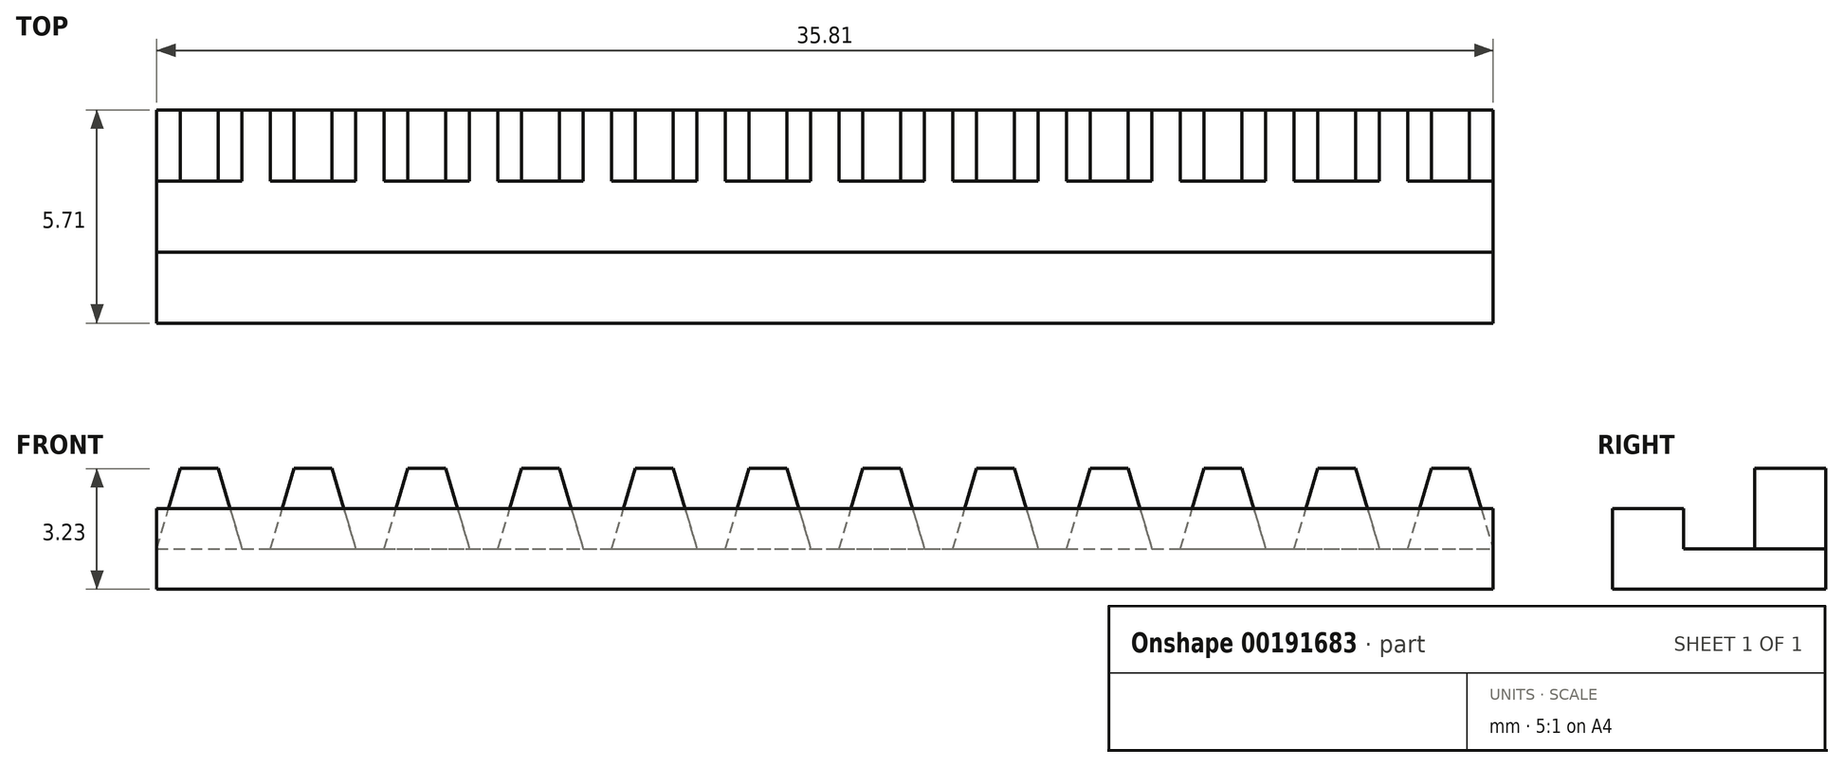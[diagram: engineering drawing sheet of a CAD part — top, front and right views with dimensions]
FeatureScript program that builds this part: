
annotation { "Feature Type Name" : "Feature", "Feature Type Description" : "" }
export const myFeature = defineFeature(function(context is Context, id is Id, definition is map)
    precondition{}
    {
        {
            var Q0;
            Q0=qCreatedBy(makeId("Front.planeOp"),FACE);
            var sketch = newSketch(context, id + "F0", { "sketchPlane" : qUnion([Q0])});
            skLineSegment(sketch, "E0.bottom", {"start": v(-38.44, 14.74) * mm, "end": v(33.18, 14.74) * mm});
            skLineSegment(sketch, "E0.top", {"start": v(-38.44, 16.9) * mm, "end": v(33.18, 16.9) * mm});
            skLineSegment(sketch, "E0.left", {"start": v(-38.44, 14.74) * mm, "end": v(-38.44, 16.9) * mm});
            skLineSegment(sketch, "E1", {"start": v(-38.44, 16.9) * mm, "end": v(-37.17, 21.21) * mm});
            skLineSegment(sketch, "E2", {"start": v(-37.17, 21.21) * mm, "end": v(-35.14, 21.21) * mm});
            skLineSegment(sketch, "E3", {"start": v(-35.14, 21.21) * mm, "end": v(-33.87, 16.9) * mm});
            skLineSegment(sketch, "E4", {"start": v(-38.44, 16.9) * mm, "end": v(-33.87, 16.9) * mm});
            skLineSegment(sketch, "E5", {"start": v(-36.16, 21.21) * mm, "end": v(-36.16, 16.9) * mm, "construction": true});
            skLineSegment(sketch, "E6", {"start": v(33.18, 14.74) * mm, "end": v(33.18, 16.9) * mm});
            skLineSegment(sketch, "E7.1.0.0", {"start": v(-29.05, 21.21) * mm, "end": v(-27.78, 16.9) * mm});
            skLineSegment(sketch, "E7.1.0.1", {"start": v(-32.35, 16.9) * mm, "end": v(-31.08, 21.21) * mm});
            skLineSegment(sketch, "E7.1.0.2", {"start": v(-31.08, 21.21) * mm, "end": v(-29.05, 21.21) * mm});
            skLineSegment(sketch, "E7.2.0.0", {"start": v(-22.95, 21.21) * mm, "end": v(-21.68, 16.9) * mm});
            skLineSegment(sketch, "E7.2.0.1", {"start": v(-26.25, 16.9) * mm, "end": v(-24.98, 21.21) * mm});
            skLineSegment(sketch, "E7.2.0.2", {"start": v(-24.98, 21.21) * mm, "end": v(-22.95, 21.21) * mm});
            skLineSegment(sketch, "E7.3.0.0", {"start": v(-16.85, 21.21) * mm, "end": v(-15.58, 16.9) * mm});
            skLineSegment(sketch, "E7.3.0.1", {"start": v(-20.16, 16.9) * mm, "end": v(-18.89, 21.21) * mm});
            skLineSegment(sketch, "E7.3.0.2", {"start": v(-18.89, 21.21) * mm, "end": v(-16.85, 21.21) * mm});
            skLineSegment(sketch, "E7.4.0.0", {"start": v(-10.76, 21.21) * mm, "end": v(-9.49, 16.9) * mm});
            skLineSegment(sketch, "E7.4.0.1", {"start": v(-14.06, 16.9) * mm, "end": v(-12.8, 21.21) * mm});
            skLineSegment(sketch, "E7.4.0.2", {"start": v(-12.8, 21.21) * mm, "end": v(-10.76, 21.21) * mm});
            skLineSegment(sketch, "E7.5.0.0", {"start": v(-4.66, 21.21) * mm, "end": v(-3.4, 16.9) * mm});
            skLineSegment(sketch, "E7.5.0.1", {"start": v(-7.96, 16.9) * mm, "end": v(-6.7, 21.21) * mm});
            skLineSegment(sketch, "E7.5.0.2", {"start": v(-6.7, 21.21) * mm, "end": v(-4.66, 21.21) * mm});
            skLineSegment(sketch, "E7.6.0.0", {"start": v(1.43, 21.21) * mm, "end": v(2.7, 16.9) * mm});
            skLineSegment(sketch, "E7.6.0.1", {"start": v(-1.87, 16.9) * mm, "end": v(-0.6, 21.21) * mm});
            skLineSegment(sketch, "E7.6.0.2", {"start": v(-0.6, 21.21) * mm, "end": v(1.43, 21.21) * mm});
            skLineSegment(sketch, "E7.7.0.0", {"start": v(7.53, 21.21) * mm, "end": v(8.8, 16.9) * mm});
            skLineSegment(sketch, "E7.7.0.1", {"start": v(4.23, 16.9) * mm, "end": v(5.5, 21.21) * mm});
            skLineSegment(sketch, "E7.7.0.2", {"start": v(5.5, 21.21) * mm, "end": v(7.53, 21.21) * mm});
            skLineSegment(sketch, "E7.8.0.0", {"start": v(13.63, 21.21) * mm, "end": v(14.9, 16.9) * mm});
            skLineSegment(sketch, "E7.8.0.1", {"start": v(10.32, 16.9) * mm, "end": v(11.6, 21.21) * mm});
            skLineSegment(sketch, "E7.8.0.2", {"start": v(11.6, 21.21) * mm, "end": v(13.63, 21.21) * mm});
            skLineSegment(sketch, "E7.9.0.0", {"start": v(19.72, 21.21) * mm, "end": v(21, 16.9) * mm});
            skLineSegment(sketch, "E7.9.0.1", {"start": v(16.42, 16.9) * mm, "end": v(17.69, 21.21) * mm});
            skLineSegment(sketch, "E7.9.0.2", {"start": v(17.69, 21.21) * mm, "end": v(19.72, 21.21) * mm});
            skLineSegment(sketch, "E7.10.0.0", {"start": v(25.82, 21.21) * mm, "end": v(27.09, 16.9) * mm});
            skLineSegment(sketch, "E7.10.0.1", {"start": v(22.52, 16.9) * mm, "end": v(23.79, 21.21) * mm});
            skLineSegment(sketch, "E7.10.0.2", {"start": v(23.79, 21.21) * mm, "end": v(25.82, 21.21) * mm});
            skLineSegment(sketch, "E7.11.0.0", {"start": v(31.91, 21.21) * mm, "end": v(33.18, 16.9) * mm});
            skLineSegment(sketch, "E7.11.0.1", {"start": v(28.61, 16.9) * mm, "end": v(29.88, 21.21) * mm});
            skLineSegment(sketch, "E7.11.0.2", {"start": v(29.88, 21.21) * mm, "end": v(31.91, 21.21) * mm});
            skLineSegment(sketch, "E7.direction1", {"start": v(-38.44, 16.9) * mm, "end": v(-32.35, 16.9) * mm, "construction": true});
            skPoint(sketch, "E8.centerSnap0", {"position": v(-38.44, 15.82) * mm});
            skSolve(sketch);
        }
        {
            var Q0;
            Q0=qSketchRegion(id+"F0",true);
            extrude(context, id + "F1", {"entities" : qUnion([Q0]), "depth" : 3.8 * mm});
        }
        {
            var Q0;
            Q0=qCreatedBy(makeId("Right.planeOp"),FACE);
            var Q1;
            Q1=makeQuery(id+"F1.opExtrude","CAP_VERTEX",VERTEX,{"disambiguationData":[OSD([sQuery(id+"F0.wireOp",EDGE,"E0.bottom"),sQuery(id+"F0.wireOp",EDGE,"E6")])],"isStart":false});
            cPlane(context, id + "F2", {"entities" : qUnion([Q0, Q1]), "cplaneType" : CPlaneType.PLANE_POINT, "offset" : 25.4 * mm, "width" : 152.4 * mm, "height" : 152.4 * mm});
        }
        {
            var Q0;
            Q0=qCreatedBy(id+"F2.planeOp",FACE);
            var sketch = newSketch(context, id + "F3", { "sketchPlane" : qUnion([Q0])});
            skLineSegment(sketch, "E9.0", {"start": v(-3.81, 14.74) * mm, "end": v(-3.81, 16.9) * mm});
            skLineSegment(sketch, "E10", {"start": v(-15.24, 16.9) * mm, "end": v(-11.43, 16.9) * mm});
            skLineSegment(sketch, "E11", {"start": v(-7.62, 16.9) * mm, "end": v(-7.62, 19.05) * mm});
            skLineSegment(sketch, "E12", {"start": v(-7.62, 19.05) * mm, "end": v(-11.43, 19.05) * mm});
            skLineSegment(sketch, "E13", {"start": v(-11.43, 19.05) * mm, "end": v(-11.43, 16.9) * mm});
            skLineSegment(sketch, "E14.trimOffspring", {"start": v(-7.62, 16.9) * mm, "end": v(-3.81, 16.9) * mm});
            skLineSegment(sketch, "E15", {"start": v(-3.81, 14.74) * mm, "end": v(-15.24, 14.74) * mm});
            skLineSegment(sketch, "E16", {"start": v(-15.24, 14.74) * mm, "end": v(-15.24, 16.9) * mm});
            skLineSegment(sketch, "E17", {"start": v(-11.43, 16.9) * mm, "end": v(-11.43, 14.74) * mm});
            skSolve(sketch);
        }
        {
            var Q0;
            {var subQ0=sQuery(id+"F3.wireOp",EDGE,"E9.0");Q0=makeQuery(id+"F3.imprint","IMPRINT",FACE,{"disambiguationData":[TD([[makeQuery(id+"F3.imprint","IMPRINT",EDGE,{"derivedFrom":subQ0}),1.0]])]});}
            var Q1;
            Q1=makeQuery(id+"F1.opExtrude","SWEPT_FACE",FACE,{"disambiguationData":[OSD([sQuery(id+"F0.wireOp",EDGE,"E0.left")])]});
            extrude(context, id + "F4", {"entities" : qUnion([Q0]), "operationType" : NewBodyOperationType.ADD, "endBound" : BoundingType.UP_TO_SURFACE, "oppositeDirection" : true, "endBoundEntityFace" : qUnion([Q1]), "depth" : 33.02 * mm});
        }
        {
            var Q0;
            Q0=makeQuery(id+"F1.opExtrude","SWEPT_BODY",BODY,{"disambiguationData":[OSD([sQuery(id+"F0.wireOp",EDGE,"E0.bottom"),sQuery(id+"F0.wireOp",EDGE,"E0.top"),sQuery(id+"F0.wireOp",EDGE,"E0.left"),sQuery(id+"F0.wireOp",EDGE,"E1"),sQuery(id+"F0.wireOp",EDGE,"E2"),sQuery(id+"F0.wireOp",EDGE,"E3"),sQuery(id+"F0.wireOp",EDGE,"E6"),sQuery(id+"F0.wireOp",EDGE,"E7.1.0.0"),sQuery(id+"F0.wireOp",EDGE,"E7.1.0.1"),sQuery(id+"F0.wireOp",EDGE,"E7.1.0.2"),sQuery(id+"F0.wireOp",EDGE,"E7.2.0.0"),sQuery(id+"F0.wireOp",EDGE,"E7.2.0.1"),sQuery(id+"F0.wireOp",EDGE,"E7.2.0.2"),sQuery(id+"F0.wireOp",EDGE,"E7.3.0.0"),sQuery(id+"F0.wireOp",EDGE,"E7.3.0.1"),sQuery(id+"F0.wireOp",EDGE,"E7.3.0.2"),sQuery(id+"F0.wireOp",EDGE,"E7.4.0.0"),sQuery(id+"F0.wireOp",EDGE,"E7.4.0.1"),sQuery(id+"F0.wireOp",EDGE,"E7.4.0.2"),sQuery(id+"F0.wireOp",EDGE,"E7.5.0.0"),sQuery(id+"F0.wireOp",EDGE,"E7.5.0.1"),sQuery(id+"F0.wireOp",EDGE,"E7.5.0.2"),sQuery(id+"F0.wireOp",EDGE,"E7.6.0.0"),sQuery(id+"F0.wireOp",EDGE,"E7.6.0.1"),sQuery(id+"F0.wireOp",EDGE,"E7.6.0.2"),sQuery(id+"F0.wireOp",EDGE,"E7.7.0.0"),sQuery(id+"F0.wireOp",EDGE,"E7.7.0.1"),sQuery(id+"F0.wireOp",EDGE,"E7.7.0.2"),sQuery(id+"F0.wireOp",EDGE,"E7.8.0.0"),sQuery(id+"F0.wireOp",EDGE,"E7.8.0.1"),sQuery(id+"F0.wireOp",EDGE,"E7.8.0.2"),sQuery(id+"F0.wireOp",EDGE,"E7.9.0.0"),sQuery(id+"F0.wireOp",EDGE,"E7.9.0.1"),sQuery(id+"F0.wireOp",EDGE,"E7.9.0.2"),sQuery(id+"F0.wireOp",EDGE,"E7.10.0.0"),sQuery(id+"F0.wireOp",EDGE,"E7.10.0.1"),sQuery(id+"F0.wireOp",EDGE,"E7.10.0.2"),sQuery(id+"F0.wireOp",EDGE,"E7.11.0.0"),sQuery(id+"F0.wireOp",EDGE,"E7.11.0.1"),sQuery(id+"F0.wireOp",EDGE,"E7.11.0.2")])]});
            var Q1;
            Q1=makeQuery(id+"F1.opExtrude","CAP_VERTEX",VERTEX,{"disambiguationData":[OSD([sQuery(id+"F0.wireOp",EDGE,"E0.bottom"),sQuery(id+"F0.wireOp",EDGE,"E6")])],"isStart":true});
            transform(context, id + "F5", {"entities" : qUnion([Q0]), "transformType" : TransformType.SCALE_UNIFORMLY, "scale" : .5, "scalePoint" : qUnion([Q1]), "makeCopy" : false});
        }
    });
